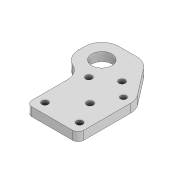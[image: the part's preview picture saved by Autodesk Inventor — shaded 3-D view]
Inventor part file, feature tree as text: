
AUTODESK INVENTOR PART (.ipt)
format: ipt  version: 2022 (Build 260153000, 153)  size: 176,128 bytes
history: native  units: mm
features: sketch x3, extrude x2, fillet x2, projected_geometry x2
ambient origin geometry x8: Origin, YZ Plane, XZ Plane, XY Plane, X Axis, Y Axis, Z Axis, Center Point
bodies: Solid1 (feature_tree)
feature tree (9):
  extrude  "Extrusion1"  Depth=18.0mm
  fillet  "Fillet1"  Radius=2.0mm
  fillet  "Fillet2"  Radius=2.2mm
  extrude  "Extrusion2"  Depth=3.0mm
  sketch  "Sketch2"  dims[d4=3.0mm d5=1.5mm]
  sketch  "Sketch1"  dims[d0=18.2mm d1=18.0mm d2=2.0mm d3=2.2mm]
  projected_geometry  "Projected Loop1"
  sketch  "Sketch3"  dims[d6=2.0mm d7=2.2mm d8=2.2mm d9=1.5mm d10=3.0mm d11=3.0mm d12=1.5mm d13=1.5mm d14=3.0mm d15=3.0mm d16=0.0mm d17=7.0mm d19=6.0mm d20=7.0mm d22=7.0mm d23=18.0mm d24=8.0mm d25=2.0mm d26=6.0mm d29=2.3mm d32=100.0mm d33=0.0mm d34=11.0mm d35=11.1mm d36=2.2mm d37=3.0mm d38=10.0mm]
  projected_geometry  "Projected Loop2"
